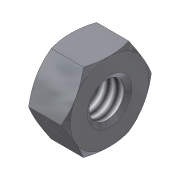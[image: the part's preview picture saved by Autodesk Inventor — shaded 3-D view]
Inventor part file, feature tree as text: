
AUTODESK INVENTOR PART (.ipt)
format: ipt  version: 2013 (Build 170138000, 138)  size: 146,432 bytes
history: native  units: mm (DEFAULTED — no unit token found)
features: sketch x3, chamfer x1, hole x1
ambient origin geometry x8: Origin, YZ Plane, XZ Plane, XY Plane, X Axis, Y Axis, Z Axis, Center Point
bodies: Solid1 (feature_tree), Body (feature_tree)
feature tree (5):
  chamfer  "Chamfer1"  Angle=30.0deg  [1 undecoded]
  hole  "Thread"  [1 undecoded]
  sketch  "Sketch1"  dims[d0=12.83161mm]
  sketch  "Sketch2"  dims[d1=5.5626mm]
  sketch  "Sketch3"  dims[d2=0.0mm d3=30.0deg d4=30.0deg d5=11.1125mm d6=11.1125mm d7=90.0deg d25=4.9784mm d26=6.0mm d27=4.0mm d28=2.0mm d29=14.3117mm d30=8.0mm d31=20.594885mm d8=0.687408mm d9=30.0deg d10=0.687408mm d11=30.0deg d13=0.0mm d14=0.0mm d39=0.0mm d40=0.687408mm d41=0.687408mm]
note: 2 required parameter values undecoded (feature->parameter linkage not recoverable at this tier; creation-order binding heuristic only, values carry confidence <= 0.55)
